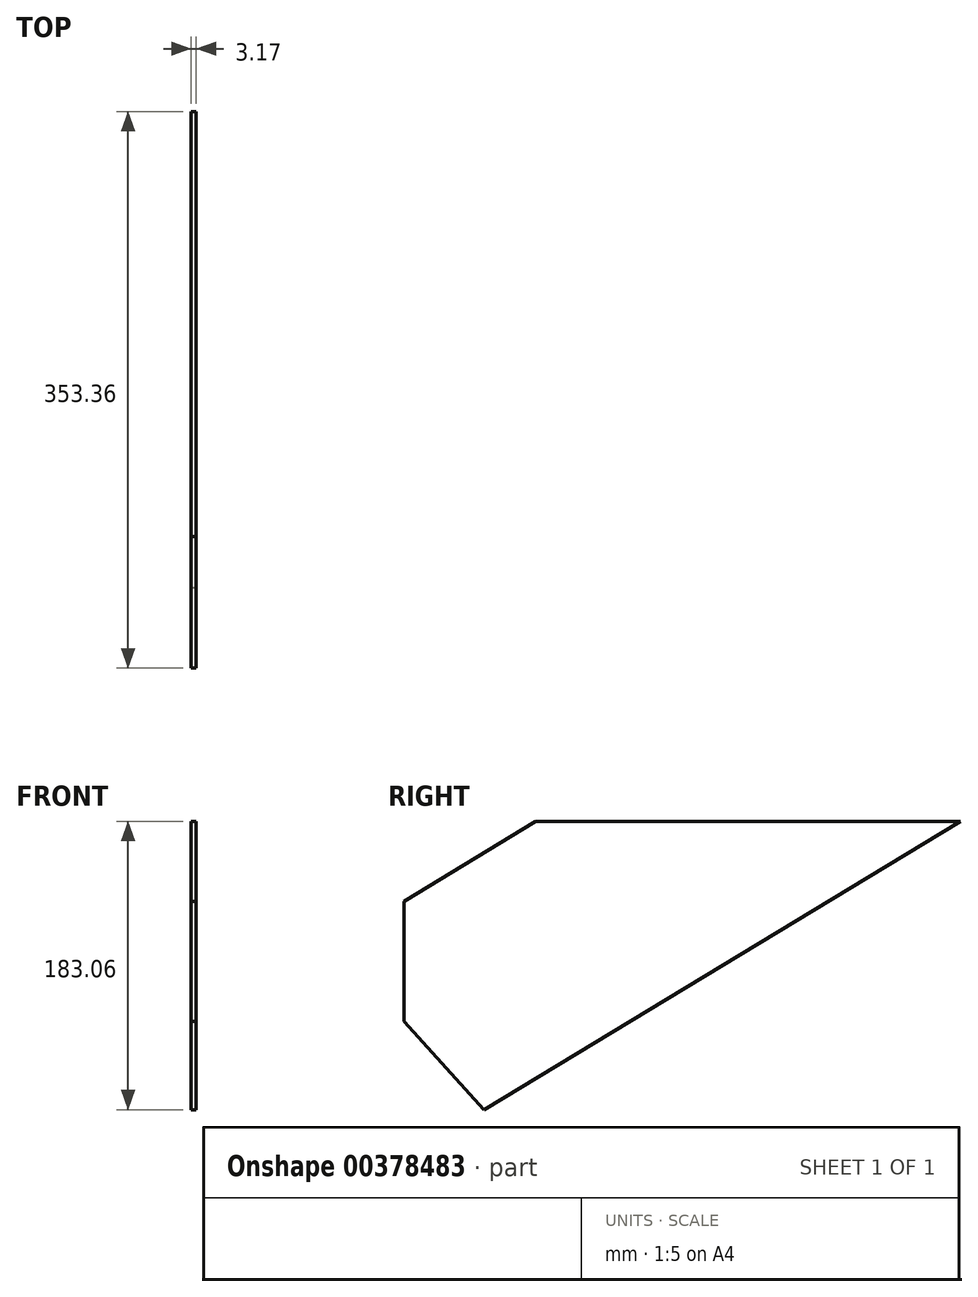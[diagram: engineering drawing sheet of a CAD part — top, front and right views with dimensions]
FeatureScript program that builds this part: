
annotation { "Feature Type Name" : "Feature", "Feature Type Description" : "" }
export const myFeature = defineFeature(function(context is Context, id is Id, definition is map)
    precondition{}
    {
        {
            var Q0;
            Q0=qCreatedBy(makeId("Right.planeOp"),FACE);
            var sketch = newSketch(context, id + "F0", { "sketchPlane" : qUnion([Q0])});
            skLineSegment(sketch, "E0.bottom", {"start": v(-93.2, 88.9) * mm, "end": v(176.68, 88.9) * mm});
            skLineSegment(sketch, "E0.left", {"start": v(-176.68, 38.1) * mm, "end": v(-176.68, -38.1) * mm});
            skPoint(sketch, "E0.middle", {"position": v(0, 0) * mm});
            skLineSegment(sketch, "E1", {"start": v(176.68, 88.9) * mm, "end": v(-125.88, -94.16) * mm});
            skLineSegment(sketch, "E2", {"start": v(-93.2, 88.9) * mm, "end": v(-176.68, 38.1) * mm});
            skLineSegment(sketch, "E3", {"start": v(-176.68, -38.1) * mm, "end": v(-125.88, -94.16) * mm});
            skPoint(sketch, "E4.orphan", {"position": v(176.68, -88.9) * mm});
            skPoint(sketch, "E0.top.start.orphan", {"position": v(-176.68, -88.9) * mm});
            skPoint(sketch, "E5.orphan", {"position": v(-176.68, 88.9) * mm});
            skSolve(sketch);
        }
        {
            var Q0;
            Q0 = qSketchRegion(id + "F0", true);
            extrude(context, id + "F1", {"entities" : qUnion([Q0]), "depth" : 3.17 * mm});
        }
    });
